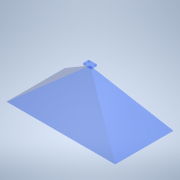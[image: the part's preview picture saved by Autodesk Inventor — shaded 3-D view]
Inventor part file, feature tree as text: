
AUTODESK INVENTOR PART (.ipt)
format: ipt  version: 2022.6 (Build 266554000, 554)  size: 141,312 bytes
history: native  units: mm
features: sketch x6, extrude x2, plane x1, loft x1, hole x1
ambient origin geometry x8: Origin, YZ Plane, XZ Plane, XY Plane, X Axis, Y Axis, Z Axis, Center Point
bodies: Solid1 (feature_tree)
feature tree (11):
  sketch  "Sketch2"  dims[d0=370.5mm d1=198.6mm]
  plane  "Work Plane1"
  loft  "Loft1"
  extrude  "Extrusion1"  TaperAngle=0.0deg  [1 undecoded]
  hole  "Hole1"  [1 undecoded]
  extrude  "Extrusion2"  Depth=5.0mm TaperAngle=0.0deg
  sketch  "Sketch7"  dims[d12=13.0mm d13=3.4mm d14=6.0mm d15=4.0mm d16=2.0mm d17=90.0deg d18=8.0mm d19=20.594885mm d20=2.0mm d21=1.0mm d22=200.0mm d23=0.0mm]
  sketch  "Sketch3"  dims[d2=150.0mm d3=0.0mm d4=90.0deg]
  sketch  "Sketch4"  dims[d5=0.0mm d6=90.0deg d7=28.0mm]
  sketch  "Sketch5"  dims[d8=20.0mm d9=5.0mm d10=0.0mm]
  sketch  "Sketch6"  dims[d11=21.0mm]
note: 2 required parameter values undecoded (feature->parameter linkage not recoverable at this tier; creation-order binding heuristic only, values carry confidence <= 0.55)
